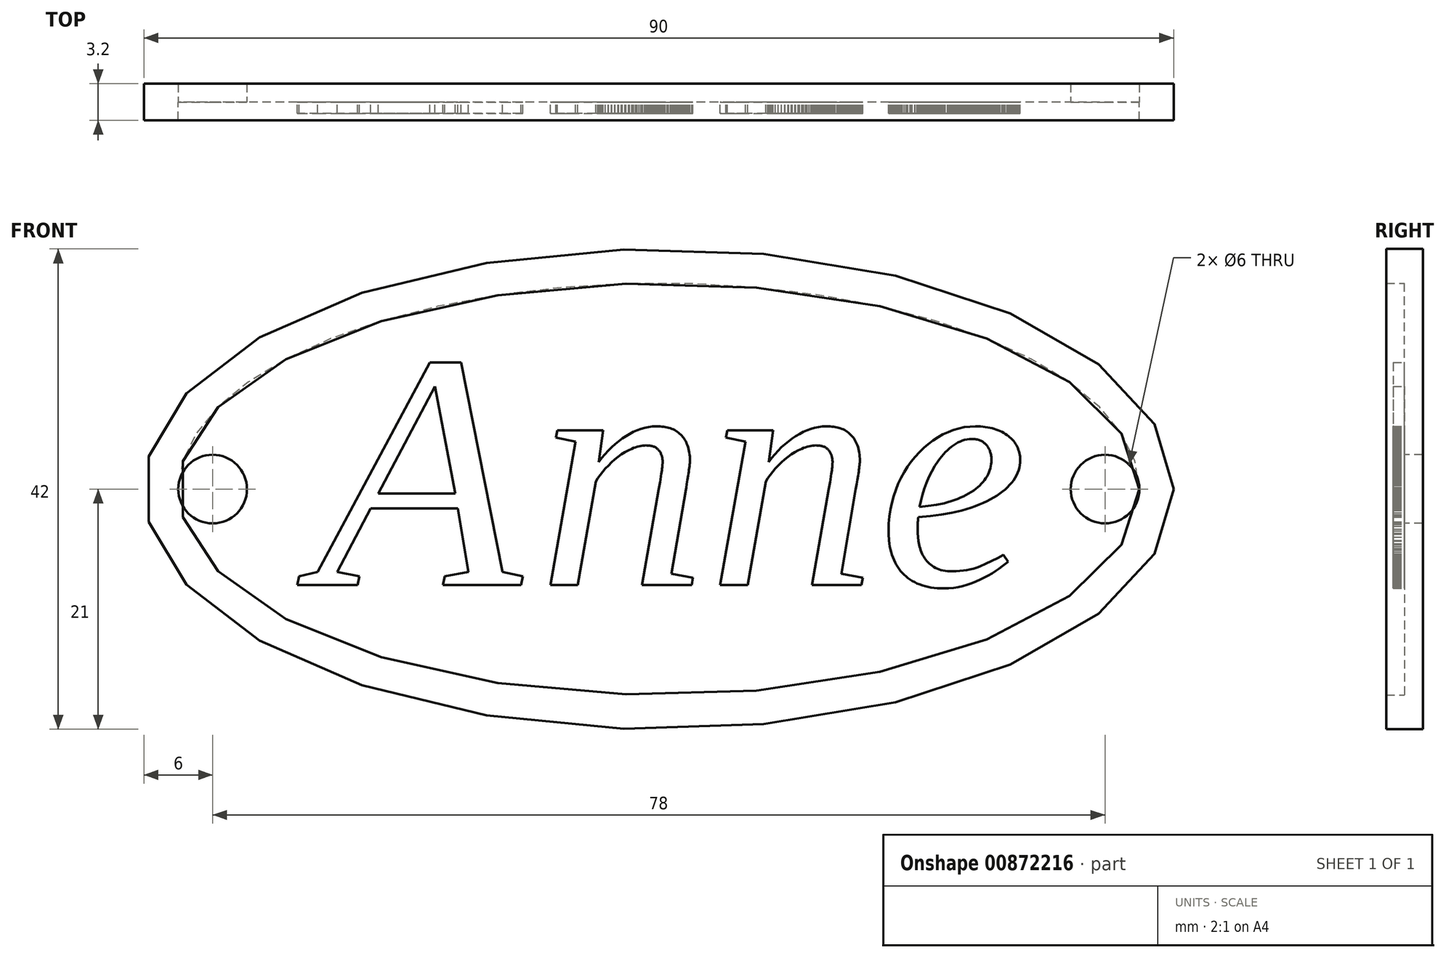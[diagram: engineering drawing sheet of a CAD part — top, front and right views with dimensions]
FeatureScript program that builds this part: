
annotation { "Feature Type Name" : "Feature", "Feature Type Description" : "" }
export const myFeature = defineFeature(function(context is Context, id is Id, definition is map)
    precondition{}
    {
        {
            var Q0;
            Q0=qCreatedBy(makeId("Front.planeOp"),FACE);
            var sketch = newSketch(context, id + "F0", { "sketchPlane" : qUnion([Q0])});
            skEllipse(sketch, "E0", {"center": v(0, 0) * mm, "majorRadius": 42 * mm, "minorRadius": 18 * mm, "majorAxis": v(1, 0)});
            skEllipse(sketch, "E1", {"center": v(0, 0) * mm, "majorRadius": 45 * mm, "minorRadius": 21 * mm, "majorAxis": v(1, 0)});
            skLineSegment(sketch, "E2", {"start": v(-81.12, 0) * mm, "end": v(85, 0) * mm, "construction": true});
            skPoint(sketch, "E2.startSnap0", {"position": v(-45, 0) * mm});
            skPoint(sketch, "E2.endSnap0", {"position": v(45, 0) * mm});
            skCircle(sketch, "E3", {"center": v(-39, 0) * mm, "radius": 3 * mm});
            skCircle(sketch, "E4", {"center": v(39, 0) * mm, "radius": 3 * mm});
            skLineSegment(sketch, "E5", {"start": v(-26.18, -7.64) * mm, "end": v(-26.32, -8.4) * mm});
            skLineSegment(sketch, "E6", {"start": v(-26.32, -8.4) * mm, "end": v(-31.6, -8.4) * mm});
            skLineSegment(sketch, "E7", {"start": v(-31.6, -8.4) * mm, "end": v(-31.45, -7.64) * mm});
            skLineSegment(sketch, "E8", {"start": v(-31.45, -7.64) * mm, "end": v(-29.84, -7.25) * mm});
            skLineSegment(sketch, "E9", {"start": v(-29.84, -7.25) * mm, "end": v(-20.02, 11.06) * mm});
            skLineSegment(sketch, "E10", {"start": v(-20.02, 11.06) * mm, "end": v(-17.27, 11.06) * mm});
            skLineSegment(sketch, "E11", {"start": v(-17.27, 11.06) * mm, "end": v(-13.67, -7.25) * mm});
            skLineSegment(sketch, "E12", {"start": v(-13.67, -7.25) * mm, "end": v(-11.87, -7.64) * mm});
            skLineSegment(sketch, "E13", {"start": v(-11.87, -7.64) * mm, "end": v(-12.03, -8.4) * mm});
            skLineSegment(sketch, "E14", {"start": v(-12.03, -8.4) * mm, "end": v(-18.87, -8.4) * mm});
            skLineSegment(sketch, "E15", {"start": v(-18.87, -8.4) * mm, "end": v(-18.71, -7.64) * mm});
            skLineSegment(sketch, "E16", {"start": v(-18.71, -7.64) * mm, "end": v(-16.65, -7.25) * mm});
            skLineSegment(sketch, "E17", {"start": v(-16.65, -7.25) * mm, "end": v(-17.57, -1.68) * mm});
            skLineSegment(sketch, "E18", {"start": v(-17.57, -1.68) * mm, "end": v(-25.17, -1.68) * mm});
            skLineSegment(sketch, "E19", {"start": v(-25.17, -1.68) * mm, "end": v(-28.12, -7.25) * mm});
            skLineSegment(sketch, "E20", {"start": v(-28.12, -7.25) * mm, "end": v(-26.18, -7.64) * mm});
            skLineSegment(sketch, "E21", {"start": v(-19.57, 8.99) * mm, "end": v(-24.53, -0.38) * mm});
            skLineSegment(sketch, "E22", {"start": v(-24.53, -0.38) * mm, "end": v(-17.8, -0.38) * mm});
            skLineSegment(sketch, "E23", {"start": v(-17.8, -0.38) * mm, "end": v(-19.57, 8.99) * mm});
            skLineSegment(sketch, "E24", {"start": v(0.33, 2.37) * mm, "end": v(0.33, 2.52) * mm});
            skLineSegment(sketch, "E25", {"start": v(0.33, 2.52) * mm, "end": v(0.32, 2.6) * mm});
            skLineSegment(sketch, "E26", {"start": v(0.32, 2.6) * mm, "end": v(0.3, 2.67) * mm});
            skLineSegment(sketch, "E27", {"start": v(0.3, 2.67) * mm, "end": v(0.3, 2.75) * mm});
            skLineSegment(sketch, "E28", {"start": v(0.3, 2.75) * mm, "end": v(0.28, 2.82) * mm});
            skLineSegment(sketch, "E29", {"start": v(0.28, 2.82) * mm, "end": v(0.26, 2.89) * mm});
            skLineSegment(sketch, "E30", {"start": v(0.26, 2.89) * mm, "end": v(0.24, 2.95) * mm});
            skLineSegment(sketch, "E31", {"start": v(0.24, 2.95) * mm, "end": v(0.22, 3.02) * mm});
            skLineSegment(sketch, "E32", {"start": v(0.22, 3.02) * mm, "end": v(0.2, 3.08) * mm});
            skLineSegment(sketch, "E33", {"start": v(0.2, 3.08) * mm, "end": v(0.17, 3.14) * mm});
            skLineSegment(sketch, "E34", {"start": v(0.17, 3.14) * mm, "end": v(0.14, 3.2) * mm});
            skLineSegment(sketch, "E35", {"start": v(0.14, 3.2) * mm, "end": v(0.1, 3.26) * mm});
            skLineSegment(sketch, "E36", {"start": v(0.1, 3.26) * mm, "end": v(0.07, 3.31) * mm});
            skLineSegment(sketch, "E37", {"start": v(0.07, 3.31) * mm, "end": v(0.03, 3.36) * mm});
            skLineSegment(sketch, "E38", {"start": v(0.03, 3.36) * mm, "end": v(-0.01, 3.42) * mm});
            skLineSegment(sketch, "E39", {"start": v(-0.01, 3.42) * mm, "end": v(-0.06, 3.46) * mm});
            skLineSegment(sketch, "E40", {"start": v(-0.06, 3.46) * mm, "end": v(-0.1, 3.51) * mm});
            skLineSegment(sketch, "E41", {"start": v(-0.1, 3.51) * mm, "end": v(-0.16, 3.55) * mm});
            skLineSegment(sketch, "E42", {"start": v(-0.16, 3.55) * mm, "end": v(-0.21, 3.6) * mm});
            skLineSegment(sketch, "E43", {"start": v(-0.21, 3.6) * mm, "end": v(-0.27, 3.63) * mm});
            skLineSegment(sketch, "E44", {"start": v(-0.27, 3.63) * mm, "end": v(-0.33, 3.66) * mm});
            skLineSegment(sketch, "E45", {"start": v(-0.33, 3.66) * mm, "end": v(-0.4, 3.7) * mm});
            skLineSegment(sketch, "E46", {"start": v(-0.4, 3.7) * mm, "end": v(-0.46, 3.72) * mm});
            skLineSegment(sketch, "E47", {"start": v(-0.46, 3.72) * mm, "end": v(-0.53, 3.74) * mm});
            skLineSegment(sketch, "E48", {"start": v(-0.53, 3.74) * mm, "end": v(-0.6, 3.76) * mm});
            skLineSegment(sketch, "E49", {"start": v(-0.6, 3.76) * mm, "end": v(-0.68, 3.78) * mm});
            skLineSegment(sketch, "E50", {"start": v(-0.68, 3.78) * mm, "end": v(-0.76, 3.8) * mm});
            skLineSegment(sketch, "E51", {"start": v(-0.76, 3.8) * mm, "end": v(-0.84, 3.8) * mm});
            skLineSegment(sketch, "E52", {"start": v(-0.84, 3.8) * mm, "end": v(-0.93, 3.81) * mm});
            skLineSegment(sketch, "E53", {"start": v(-0.93, 3.81) * mm, "end": v(-1.02, 3.82) * mm});
            skLineSegment(sketch, "E54", {"start": v(-1.02, 3.82) * mm, "end": v(-1.1, 3.82) * mm});
            skLineSegment(sketch, "E55", {"start": v(-1.1, 3.82) * mm, "end": v(-1.26, 3.81) * mm});
            skLineSegment(sketch, "E56", {"start": v(-1.26, 3.81) * mm, "end": v(-1.41, 3.8) * mm});
            skLineSegment(sketch, "E57", {"start": v(-1.41, 3.8) * mm, "end": v(-1.57, 3.78) * mm});
            skLineSegment(sketch, "E58", {"start": v(-1.57, 3.78) * mm, "end": v(-1.72, 3.75) * mm});
            skLineSegment(sketch, "E59", {"start": v(-1.72, 3.75) * mm, "end": v(-1.88, 3.7) * mm});
            skLineSegment(sketch, "E60", {"start": v(-1.88, 3.7) * mm, "end": v(-2.03, 3.66) * mm});
            skLineSegment(sketch, "E61", {"start": v(-2.03, 3.66) * mm, "end": v(-2.19, 3.6) * mm});
            skLineSegment(sketch, "E62", {"start": v(-2.19, 3.6) * mm, "end": v(-2.35, 3.53) * mm});
            skLineSegment(sketch, "E63", {"start": v(-2.35, 3.53) * mm, "end": v(-2.66, 3.38) * mm});
            skLineSegment(sketch, "E64", {"start": v(-2.66, 3.38) * mm, "end": v(-2.97, 3.21) * mm});
            skLineSegment(sketch, "E65", {"start": v(-2.97, 3.21) * mm, "end": v(-3.27, 3.02) * mm});
            skLineSegment(sketch, "E66", {"start": v(-3.27, 3.02) * mm, "end": v(-3.57, 2.81) * mm});
            skLineSegment(sketch, "E67", {"start": v(-3.57, 2.81) * mm, "end": v(-3.86, 2.58) * mm});
            skLineSegment(sketch, "E68", {"start": v(-3.86, 2.58) * mm, "end": v(-4.14, 2.33) * mm});
            skLineSegment(sketch, "E69", {"start": v(-4.14, 2.33) * mm, "end": v(-4.4, 2.07) * mm});
            skLineSegment(sketch, "E70", {"start": v(-4.4, 2.07) * mm, "end": v(-4.66, 1.79) * mm});
            skLineSegment(sketch, "E71", {"start": v(-4.66, 1.79) * mm, "end": v(-4.9, 1.5) * mm});
            skLineSegment(sketch, "E72", {"start": v(-4.9, 1.5) * mm, "end": v(-5.13, 1.23) * mm});
            skLineSegment(sketch, "E73", {"start": v(-5.13, 1.23) * mm, "end": v(-5.33, 0.95) * mm});
            skLineSegment(sketch, "E74", {"start": v(-5.33, 0.95) * mm, "end": v(-5.51, 0.67) * mm});
            skLineSegment(sketch, "E75", {"start": v(-5.51, 0.67) * mm, "end": v(-7.1, -8.4) * mm});
            skLineSegment(sketch, "E76", {"start": v(-7.1, -8.4) * mm, "end": v(-9.48, -8.4) * mm});
            skLineSegment(sketch, "E77", {"start": v(-9.48, -8.4) * mm, "end": v(-7.28, 4.14) * mm});
            skLineSegment(sketch, "E78", {"start": v(-7.28, 4.14) * mm, "end": v(-8.98, 4.5) * mm});
            skLineSegment(sketch, "E79", {"start": v(-8.98, 4.5) * mm, "end": v(-8.87, 5.14) * mm});
            skLineSegment(sketch, "E80", {"start": v(-8.87, 5.14) * mm, "end": v(-4.86, 5.14) * mm});
            skLineSegment(sketch, "E81", {"start": v(-4.86, 5.14) * mm, "end": v(-5.25, 2.38) * mm});
            skLineSegment(sketch, "E82", {"start": v(-5.25, 2.38) * mm, "end": v(-4.98, 2.72) * mm});
            skLineSegment(sketch, "E83", {"start": v(-4.98, 2.72) * mm, "end": v(-4.4, 3.36) * mm});
            skLineSegment(sketch, "E84", {"start": v(-4.4, 3.36) * mm, "end": v(-4.12, 3.66) * mm});
            skLineSegment(sketch, "E85", {"start": v(-4.12, 3.66) * mm, "end": v(-3.81, 3.94) * mm});
            skLineSegment(sketch, "E86", {"start": v(-3.81, 3.94) * mm, "end": v(-3.5, 4.2) * mm});
            skLineSegment(sketch, "E87", {"start": v(-3.5, 4.2) * mm, "end": v(-3.2, 4.43) * mm});
            skLineSegment(sketch, "E88", {"start": v(-3.2, 4.43) * mm, "end": v(-2.88, 4.64) * mm});
            skLineSegment(sketch, "E89", {"start": v(-2.88, 4.64) * mm, "end": v(-2.55, 4.83) * mm});
            skLineSegment(sketch, "E90", {"start": v(-2.55, 4.83) * mm, "end": v(-2.23, 5) * mm});
            skLineSegment(sketch, "E91", {"start": v(-2.23, 5) * mm, "end": v(-1.9, 5.14) * mm});
            skLineSegment(sketch, "E92", {"start": v(-1.9, 5.14) * mm, "end": v(-1.57, 5.26) * mm});
            skLineSegment(sketch, "E93", {"start": v(-1.57, 5.26) * mm, "end": v(-1.23, 5.36) * mm});
            skLineSegment(sketch, "E94", {"start": v(-1.23, 5.36) * mm, "end": v(-0.89, 5.43) * mm});
            skLineSegment(sketch, "E95", {"start": v(-0.89, 5.43) * mm, "end": v(-0.55, 5.47) * mm});
            skLineSegment(sketch, "E96", {"start": v(-0.55, 5.47) * mm, "end": v(-0.2, 5.49) * mm});
            skLineSegment(sketch, "E97", {"start": v(-0.2, 5.49) * mm, "end": v(0.12, 5.48) * mm});
            skLineSegment(sketch, "E98", {"start": v(0.12, 5.48) * mm, "end": v(0.28, 5.46) * mm});
            skLineSegment(sketch, "E99", {"start": v(0.28, 5.46) * mm, "end": v(0.43, 5.45) * mm});
            skLineSegment(sketch, "E100", {"start": v(0.43, 5.45) * mm, "end": v(0.58, 5.42) * mm});
            skLineSegment(sketch, "E101", {"start": v(0.58, 5.42) * mm, "end": v(0.72, 5.4) * mm});
            skLineSegment(sketch, "E102", {"start": v(0.72, 5.4) * mm, "end": v(0.86, 5.36) * mm});
            skLineSegment(sketch, "E103", {"start": v(0.86, 5.36) * mm, "end": v(1, 5.32) * mm});
            skLineSegment(sketch, "E104", {"start": v(1, 5.32) * mm, "end": v(1.13, 5.27) * mm});
            skLineSegment(sketch, "E105", {"start": v(1.13, 5.27) * mm, "end": v(1.26, 5.22) * mm});
            skLineSegment(sketch, "E106", {"start": v(1.26, 5.22) * mm, "end": v(1.38, 5.16) * mm});
            skLineSegment(sketch, "E107", {"start": v(1.38, 5.16) * mm, "end": v(1.5, 5.1) * mm});
            skLineSegment(sketch, "E108", {"start": v(1.5, 5.1) * mm, "end": v(1.6, 5.02) * mm});
            skLineSegment(sketch, "E109", {"start": v(1.6, 5.02) * mm, "end": v(1.72, 4.94) * mm});
            skLineSegment(sketch, "E110", {"start": v(1.72, 4.94) * mm, "end": v(1.82, 4.86) * mm});
            skLineSegment(sketch, "E111", {"start": v(1.82, 4.86) * mm, "end": v(1.91, 4.77) * mm});
            skLineSegment(sketch, "E112", {"start": v(1.91, 4.77) * mm, "end": v(2, 4.67) * mm});
            skLineSegment(sketch, "E113", {"start": v(2, 4.67) * mm, "end": v(2.1, 4.57) * mm});
            skLineSegment(sketch, "E114", {"start": v(2.1, 4.57) * mm, "end": v(2.18, 4.46) * mm});
            skLineSegment(sketch, "E115", {"start": v(2.18, 4.46) * mm, "end": v(2.26, 4.34) * mm});
            skLineSegment(sketch, "E116", {"start": v(2.26, 4.34) * mm, "end": v(2.33, 4.22) * mm});
            skLineSegment(sketch, "E117", {"start": v(2.33, 4.22) * mm, "end": v(2.4, 4.1) * mm});
            skLineSegment(sketch, "E118", {"start": v(2.4, 4.1) * mm, "end": v(2.45, 3.96) * mm});
            skLineSegment(sketch, "E119", {"start": v(2.45, 3.96) * mm, "end": v(2.5, 3.82) * mm});
            skLineSegment(sketch, "E120", {"start": v(2.5, 3.82) * mm, "end": v(2.55, 3.67) * mm});
            skLineSegment(sketch, "E121", {"start": v(2.55, 3.67) * mm, "end": v(2.6, 3.52) * mm});
            skLineSegment(sketch, "E122", {"start": v(2.6, 3.52) * mm, "end": v(2.64, 3.36) * mm});
            skLineSegment(sketch, "E123", {"start": v(2.64, 3.36) * mm, "end": v(2.67, 3.19) * mm});
            skLineSegment(sketch, "E124", {"start": v(2.67, 3.19) * mm, "end": v(2.69, 3.01) * mm});
            skLineSegment(sketch, "E125", {"start": v(2.69, 3.01) * mm, "end": v(2.7, 2.83) * mm});
            skLineSegment(sketch, "E126", {"start": v(2.7, 2.83) * mm, "end": v(2.72, 2.65) * mm});
            skLineSegment(sketch, "E127", {"start": v(2.72, 2.65) * mm, "end": v(2.72, 2.45) * mm});
            skLineSegment(sketch, "E128", {"start": v(2.72, 2.45) * mm, "end": v(2.72, 2.43) * mm});
            skLineSegment(sketch, "E129", {"start": v(2.72, 2.43) * mm, "end": v(2.72, 2.4) * mm});
            skLineSegment(sketch, "E130", {"start": v(2.72, 2.4) * mm, "end": v(2.72, 2.36) * mm});
            skLineSegment(sketch, "E131", {"start": v(2.72, 2.36) * mm, "end": v(2.71, 2.3) * mm});
            skLineSegment(sketch, "E132", {"start": v(2.71, 2.3) * mm, "end": v(2.7, 2.25) * mm});
            skLineSegment(sketch, "E133", {"start": v(2.7, 2.25) * mm, "end": v(2.7, 2.19) * mm});
            skLineSegment(sketch, "E134", {"start": v(2.7, 2.19) * mm, "end": v(2.7, 2.12) * mm});
            skLineSegment(sketch, "E135", {"start": v(2.7, 2.12) * mm, "end": v(2.69, 2.05) * mm});
            skLineSegment(sketch, "E136", {"start": v(2.69, 2.05) * mm, "end": v(2.68, 1.98) * mm});
            skLineSegment(sketch, "E137", {"start": v(2.68, 1.98) * mm, "end": v(2.66, 1.83) * mm});
            skLineSegment(sketch, "E138", {"start": v(2.66, 1.83) * mm, "end": v(2.64, 1.67) * mm});
            skLineSegment(sketch, "E139", {"start": v(2.64, 1.67) * mm, "end": v(2.62, 1.51) * mm});
            skLineSegment(sketch, "E140", {"start": v(2.62, 1.51) * mm, "end": v(2.6, 1.34) * mm});
            skLineSegment(sketch, "E141", {"start": v(2.6, 1.34) * mm, "end": v(2.56, 1.17) * mm});
            skLineSegment(sketch, "E142", {"start": v(2.56, 1.17) * mm, "end": v(2.5, 0.8) * mm});
            skLineSegment(sketch, "E143", {"start": v(2.5, 0.8) * mm, "end": v(2.48, 0.62) * mm});
            skLineSegment(sketch, "E144", {"start": v(2.48, 0.62) * mm, "end": v(2.45, 0.45) * mm});
            skLineSegment(sketch, "E145", {"start": v(2.45, 0.45) * mm, "end": v(2.39, 0.1) * mm});
            skLineSegment(sketch, "E146", {"start": v(2.39, 0.1) * mm, "end": v(2.36, -0.05) * mm});
            skLineSegment(sketch, "E147", {"start": v(2.36, -0.05) * mm, "end": v(1.1, -7.4) * mm});
            skLineSegment(sketch, "E148", {"start": v(1.1, -7.4) * mm, "end": v(2.98, -7.75) * mm});
            skLineSegment(sketch, "E149", {"start": v(2.98, -7.75) * mm, "end": v(2.86, -8.4) * mm});
            skLineSegment(sketch, "E150", {"start": v(2.86, -8.4) * mm, "end": v(-1.47, -8.4) * mm});
            skLineSegment(sketch, "E151", {"start": v(-1.47, -8.4) * mm, "end": v(0, -0.02) * mm});
            skLineSegment(sketch, "E152", {"start": v(0, -0.02) * mm, "end": v(0.03, 0.14) * mm});
            skLineSegment(sketch, "E153", {"start": v(0.03, 0.14) * mm, "end": v(0.09, 0.47) * mm});
            skLineSegment(sketch, "E154", {"start": v(0.09, 0.47) * mm, "end": v(0.11, 0.64) * mm});
            skLineSegment(sketch, "E155", {"start": v(0.11, 0.64) * mm, "end": v(0.14, 0.81) * mm});
            skLineSegment(sketch, "E156", {"start": v(0.14, 0.81) * mm, "end": v(0.2, 1.15) * mm});
            skLineSegment(sketch, "E157", {"start": v(0.2, 1.15) * mm, "end": v(0.22, 1.31) * mm});
            skLineSegment(sketch, "E158", {"start": v(0.22, 1.31) * mm, "end": v(0.24, 1.48) * mm});
            skLineSegment(sketch, "E159", {"start": v(0.24, 1.48) * mm, "end": v(0.27, 1.63) * mm});
            skLineSegment(sketch, "E160", {"start": v(0.27, 1.63) * mm, "end": v(0.29, 1.78) * mm});
            skLineSegment(sketch, "E161", {"start": v(0.29, 1.78) * mm, "end": v(0.3, 1.92) * mm});
            skLineSegment(sketch, "E162", {"start": v(0.3, 1.92) * mm, "end": v(0.3, 1.99) * mm});
            skLineSegment(sketch, "E163", {"start": v(0.3, 1.99) * mm, "end": v(0.31, 2.05) * mm});
            skLineSegment(sketch, "E164", {"start": v(0.31, 2.05) * mm, "end": v(0.32, 2.11) * mm});
            skLineSegment(sketch, "E165", {"start": v(0.32, 2.11) * mm, "end": v(0.32, 2.17) * mm});
            skLineSegment(sketch, "E166", {"start": v(0.32, 2.17) * mm, "end": v(0.33, 2.22) * mm});
            skLineSegment(sketch, "E167", {"start": v(0.33, 2.22) * mm, "end": v(0.33, 2.27) * mm});
            skLineSegment(sketch, "E168", {"start": v(0.33, 2.27) * mm, "end": v(0.33, 2.32) * mm});
            skLineSegment(sketch, "E169", {"start": v(0.33, 2.32) * mm, "end": v(0.33, 2.37) * mm});
            skLineSegment(sketch, "E170", {"start": v(15.18, 2.37) * mm, "end": v(15.18, 2.52) * mm});
            skLineSegment(sketch, "E171", {"start": v(15.18, 2.52) * mm, "end": v(15.17, 2.6) * mm});
            skLineSegment(sketch, "E172", {"start": v(15.17, 2.6) * mm, "end": v(15.16, 2.67) * mm});
            skLineSegment(sketch, "E173", {"start": v(15.16, 2.67) * mm, "end": v(15.15, 2.75) * mm});
            skLineSegment(sketch, "E174", {"start": v(15.15, 2.75) * mm, "end": v(15.14, 2.82) * mm});
            skLineSegment(sketch, "E175", {"start": v(15.14, 2.82) * mm, "end": v(15.12, 2.89) * mm});
            skLineSegment(sketch, "E176", {"start": v(15.12, 2.89) * mm, "end": v(15.1, 2.95) * mm});
            skLineSegment(sketch, "E177", {"start": v(15.1, 2.95) * mm, "end": v(15.07, 3.02) * mm});
            skLineSegment(sketch, "E178", {"start": v(15.07, 3.02) * mm, "end": v(15.05, 3.08) * mm});
            skLineSegment(sketch, "E179", {"start": v(15.05, 3.08) * mm, "end": v(15.02, 3.14) * mm});
            skLineSegment(sketch, "E180", {"start": v(15.02, 3.14) * mm, "end": v(14.99, 3.2) * mm});
            skLineSegment(sketch, "E181", {"start": v(14.99, 3.2) * mm, "end": v(14.96, 3.26) * mm});
            skLineSegment(sketch, "E182", {"start": v(14.96, 3.26) * mm, "end": v(14.92, 3.31) * mm});
            skLineSegment(sketch, "E183", {"start": v(14.92, 3.31) * mm, "end": v(14.88, 3.36) * mm});
            skLineSegment(sketch, "E184", {"start": v(14.88, 3.36) * mm, "end": v(14.84, 3.42) * mm});
            skLineSegment(sketch, "E185", {"start": v(14.84, 3.42) * mm, "end": v(14.8, 3.46) * mm});
            skLineSegment(sketch, "E186", {"start": v(14.8, 3.46) * mm, "end": v(14.75, 3.51) * mm});
            skLineSegment(sketch, "E187", {"start": v(14.75, 3.51) * mm, "end": v(14.7, 3.55) * mm});
            skLineSegment(sketch, "E188", {"start": v(14.7, 3.55) * mm, "end": v(14.64, 3.6) * mm});
            skLineSegment(sketch, "E189", {"start": v(14.64, 3.6) * mm, "end": v(14.58, 3.63) * mm});
            skLineSegment(sketch, "E190", {"start": v(14.58, 3.63) * mm, "end": v(14.52, 3.66) * mm});
            skLineSegment(sketch, "E191", {"start": v(14.52, 3.66) * mm, "end": v(14.46, 3.7) * mm});
            skLineSegment(sketch, "E192", {"start": v(14.46, 3.7) * mm, "end": v(14.4, 3.72) * mm});
            skLineSegment(sketch, "E193", {"start": v(14.4, 3.72) * mm, "end": v(14.32, 3.74) * mm});
            skLineSegment(sketch, "E194", {"start": v(14.32, 3.74) * mm, "end": v(14.25, 3.76) * mm});
            skLineSegment(sketch, "E195", {"start": v(14.25, 3.76) * mm, "end": v(14.17, 3.78) * mm});
            skLineSegment(sketch, "E196", {"start": v(14.17, 3.78) * mm, "end": v(14.1, 3.8) * mm});
            skLineSegment(sketch, "E197", {"start": v(14.1, 3.8) * mm, "end": v(14.01, 3.8) * mm});
            skLineSegment(sketch, "E198", {"start": v(14.01, 3.8) * mm, "end": v(13.93, 3.81) * mm});
            skLineSegment(sketch, "E199", {"start": v(13.93, 3.81) * mm, "end": v(13.84, 3.82) * mm});
            skLineSegment(sketch, "E200", {"start": v(13.84, 3.82) * mm, "end": v(13.74, 3.82) * mm});
            skLineSegment(sketch, "E201", {"start": v(13.74, 3.82) * mm, "end": v(13.6, 3.81) * mm});
            skLineSegment(sketch, "E202", {"start": v(13.6, 3.81) * mm, "end": v(13.44, 3.8) * mm});
            skLineSegment(sketch, "E203", {"start": v(13.44, 3.8) * mm, "end": v(13.29, 3.78) * mm});
            skLineSegment(sketch, "E204", {"start": v(13.29, 3.78) * mm, "end": v(13.13, 3.75) * mm});
            skLineSegment(sketch, "E205", {"start": v(13.13, 3.75) * mm, "end": v(12.98, 3.7) * mm});
            skLineSegment(sketch, "E206", {"start": v(12.98, 3.7) * mm, "end": v(12.82, 3.66) * mm});
            skLineSegment(sketch, "E207", {"start": v(12.82, 3.66) * mm, "end": v(12.67, 3.6) * mm});
            skLineSegment(sketch, "E208", {"start": v(12.67, 3.6) * mm, "end": v(12.5, 3.53) * mm});
            skLineSegment(sketch, "E209", {"start": v(12.5, 3.53) * mm, "end": v(12.2, 3.38) * mm});
            skLineSegment(sketch, "E210", {"start": v(12.2, 3.38) * mm, "end": v(11.88, 3.21) * mm});
            skLineSegment(sketch, "E211", {"start": v(11.88, 3.21) * mm, "end": v(11.58, 3.02) * mm});
            skLineSegment(sketch, "E212", {"start": v(11.58, 3.02) * mm, "end": v(11.28, 2.81) * mm});
            skLineSegment(sketch, "E213", {"start": v(11.28, 2.81) * mm, "end": v(11, 2.58) * mm});
            skLineSegment(sketch, "E214", {"start": v(11, 2.58) * mm, "end": v(10.72, 2.33) * mm});
            skLineSegment(sketch, "E215", {"start": v(10.72, 2.33) * mm, "end": v(10.45, 2.07) * mm});
            skLineSegment(sketch, "E216", {"start": v(10.45, 2.07) * mm, "end": v(10.19, 1.79) * mm});
            skLineSegment(sketch, "E217", {"start": v(10.2, 1.79) * mm, "end": v(9.95, 1.5) * mm});
            skLineSegment(sketch, "E218", {"start": v(9.95, 1.5) * mm, "end": v(9.73, 1.23) * mm});
            skLineSegment(sketch, "E219", {"start": v(9.73, 1.23) * mm, "end": v(9.52, 0.95) * mm});
            skLineSegment(sketch, "E220", {"start": v(9.52, 0.95) * mm, "end": v(9.34, 0.67) * mm});
            skLineSegment(sketch, "E221", {"start": v(9.34, 0.67) * mm, "end": v(7.76, -8.4) * mm});
            skLineSegment(sketch, "E222", {"start": v(7.76, -8.4) * mm, "end": v(5.37, -8.4) * mm});
            skLineSegment(sketch, "E223", {"start": v(5.37, -8.4) * mm, "end": v(7.57, 4.14) * mm});
            skLineSegment(sketch, "E224", {"start": v(7.57, 4.14) * mm, "end": v(5.87, 4.5) * mm});
            skLineSegment(sketch, "E225", {"start": v(5.87, 4.5) * mm, "end": v(5.99, 5.14) * mm});
            skLineSegment(sketch, "E226", {"start": v(5.99, 5.14) * mm, "end": v(9.99, 5.14) * mm});
            skLineSegment(sketch, "E227", {"start": v(9.99, 5.14) * mm, "end": v(9.6, 2.38) * mm});
            skLineSegment(sketch, "E228", {"start": v(9.6, 2.38) * mm, "end": v(9.88, 2.72) * mm});
            skLineSegment(sketch, "E229", {"start": v(9.88, 2.72) * mm, "end": v(10.44, 3.36) * mm});
            skLineSegment(sketch, "E230", {"start": v(10.44, 3.36) * mm, "end": v(10.74, 3.66) * mm});
            skLineSegment(sketch, "E231", {"start": v(10.74, 3.66) * mm, "end": v(11.04, 3.94) * mm});
            skLineSegment(sketch, "E232", {"start": v(11.04, 3.94) * mm, "end": v(11.35, 4.2) * mm});
            skLineSegment(sketch, "E233", {"start": v(11.35, 4.2) * mm, "end": v(11.66, 4.43) * mm});
            skLineSegment(sketch, "E234", {"start": v(11.66, 4.43) * mm, "end": v(11.97, 4.64) * mm});
            skLineSegment(sketch, "E235", {"start": v(11.97, 4.64) * mm, "end": v(12.3, 4.83) * mm});
            skLineSegment(sketch, "E236", {"start": v(12.3, 4.83) * mm, "end": v(12.63, 5) * mm});
            skLineSegment(sketch, "E237", {"start": v(12.63, 5) * mm, "end": v(12.95, 5.14) * mm});
            skLineSegment(sketch, "E238", {"start": v(12.95, 5.14) * mm, "end": v(13.28, 5.26) * mm});
            skLineSegment(sketch, "E239", {"start": v(13.28, 5.26) * mm, "end": v(13.62, 5.36) * mm});
            skLineSegment(sketch, "E240", {"start": v(13.62, 5.36) * mm, "end": v(13.96, 5.43) * mm});
            skLineSegment(sketch, "E241", {"start": v(13.96, 5.43) * mm, "end": v(14.3, 5.47) * mm});
            skLineSegment(sketch, "E242", {"start": v(14.3, 5.47) * mm, "end": v(14.65, 5.49) * mm});
            skLineSegment(sketch, "E243", {"start": v(14.65, 5.49) * mm, "end": v(14.97, 5.48) * mm});
            skLineSegment(sketch, "E244", {"start": v(14.97, 5.48) * mm, "end": v(15.13, 5.46) * mm});
            skLineSegment(sketch, "E245", {"start": v(15.13, 5.46) * mm, "end": v(15.28, 5.45) * mm});
            skLineSegment(sketch, "E246", {"start": v(15.28, 5.45) * mm, "end": v(15.43, 5.42) * mm});
            skLineSegment(sketch, "E247", {"start": v(15.43, 5.42) * mm, "end": v(15.57, 5.4) * mm});
            skLineSegment(sketch, "E248", {"start": v(15.57, 5.4) * mm, "end": v(15.71, 5.36) * mm});
            skLineSegment(sketch, "E249", {"start": v(15.71, 5.36) * mm, "end": v(15.85, 5.32) * mm});
            skLineSegment(sketch, "E250", {"start": v(15.85, 5.32) * mm, "end": v(15.98, 5.27) * mm});
            skLineSegment(sketch, "E251", {"start": v(15.98, 5.27) * mm, "end": v(16.1, 5.22) * mm});
            skLineSegment(sketch, "E252", {"start": v(16.1, 5.22) * mm, "end": v(16.23, 5.16) * mm});
            skLineSegment(sketch, "E253", {"start": v(16.23, 5.16) * mm, "end": v(16.35, 5.1) * mm});
            skLineSegment(sketch, "E254", {"start": v(16.35, 5.1) * mm, "end": v(16.46, 5.02) * mm});
            skLineSegment(sketch, "E255", {"start": v(16.46, 5.02) * mm, "end": v(16.57, 4.94) * mm});
            skLineSegment(sketch, "E256", {"start": v(16.57, 4.94) * mm, "end": v(16.67, 4.86) * mm});
            skLineSegment(sketch, "E257", {"start": v(16.67, 4.86) * mm, "end": v(16.77, 4.77) * mm});
            skLineSegment(sketch, "E258", {"start": v(16.77, 4.77) * mm, "end": v(16.86, 4.67) * mm});
            skLineSegment(sketch, "E259", {"start": v(16.86, 4.67) * mm, "end": v(16.95, 4.57) * mm});
            skLineSegment(sketch, "E260", {"start": v(16.95, 4.57) * mm, "end": v(17.03, 4.46) * mm});
            skLineSegment(sketch, "E261", {"start": v(17.03, 4.46) * mm, "end": v(17.1, 4.34) * mm});
            skLineSegment(sketch, "E262", {"start": v(17.1, 4.34) * mm, "end": v(17.18, 4.22) * mm});
            skLineSegment(sketch, "E263", {"start": v(17.18, 4.22) * mm, "end": v(17.24, 4.1) * mm});
            skLineSegment(sketch, "E264", {"start": v(17.24, 4.1) * mm, "end": v(17.3, 3.96) * mm});
            skLineSegment(sketch, "E265", {"start": v(17.3, 3.96) * mm, "end": v(17.36, 3.82) * mm});
            skLineSegment(sketch, "E266", {"start": v(17.36, 3.82) * mm, "end": v(17.4, 3.67) * mm});
            skLineSegment(sketch, "E267", {"start": v(17.4, 3.67) * mm, "end": v(17.45, 3.52) * mm});
            skLineSegment(sketch, "E268", {"start": v(17.45, 3.52) * mm, "end": v(17.49, 3.36) * mm});
            skLineSegment(sketch, "E269", {"start": v(17.49, 3.36) * mm, "end": v(17.52, 3.19) * mm});
            skLineSegment(sketch, "E270", {"start": v(17.52, 3.19) * mm, "end": v(17.54, 3.01) * mm});
            skLineSegment(sketch, "E271", {"start": v(17.54, 3.01) * mm, "end": v(17.56, 2.83) * mm});
            skLineSegment(sketch, "E272", {"start": v(17.56, 2.83) * mm, "end": v(17.57, 2.65) * mm});
            skLineSegment(sketch, "E273", {"start": v(17.57, 2.65) * mm, "end": v(17.57, 2.45) * mm});
            skLineSegment(sketch, "E274", {"start": v(17.57, 2.45) * mm, "end": v(17.57, 2.43) * mm});
            skLineSegment(sketch, "E275", {"start": v(17.57, 2.43) * mm, "end": v(17.57, 2.4) * mm});
            skLineSegment(sketch, "E276", {"start": v(17.57, 2.4) * mm, "end": v(17.57, 2.36) * mm});
            skLineSegment(sketch, "E277", {"start": v(17.57, 2.36) * mm, "end": v(17.57, 2.3) * mm});
            skLineSegment(sketch, "E278", {"start": v(17.57, 2.3) * mm, "end": v(17.56, 2.25) * mm});
            skLineSegment(sketch, "E279", {"start": v(17.56, 2.25) * mm, "end": v(17.56, 2.19) * mm});
            skLineSegment(sketch, "E280", {"start": v(17.56, 2.19) * mm, "end": v(17.55, 2.12) * mm});
            skLineSegment(sketch, "E281", {"start": v(17.55, 2.12) * mm, "end": v(17.54, 2.05) * mm});
            skLineSegment(sketch, "E282", {"start": v(17.54, 2.05) * mm, "end": v(17.53, 1.98) * mm});
            skLineSegment(sketch, "E283", {"start": v(17.53, 1.98) * mm, "end": v(17.51, 1.83) * mm});
            skLineSegment(sketch, "E284", {"start": v(17.51, 1.83) * mm, "end": v(17.5, 1.67) * mm});
            skLineSegment(sketch, "E285", {"start": v(17.5, 1.67) * mm, "end": v(17.47, 1.51) * mm});
            skLineSegment(sketch, "E286", {"start": v(17.47, 1.51) * mm, "end": v(17.44, 1.34) * mm});
            skLineSegment(sketch, "E287", {"start": v(17.44, 1.34) * mm, "end": v(17.41, 1.17) * mm});
            skLineSegment(sketch, "E288", {"start": v(17.41, 1.17) * mm, "end": v(17.36, 0.8) * mm});
            skLineSegment(sketch, "E289", {"start": v(17.36, 0.8) * mm, "end": v(17.33, 0.62) * mm});
            skLineSegment(sketch, "E290", {"start": v(17.33, 0.62) * mm, "end": v(17.3, 0.45) * mm});
            skLineSegment(sketch, "E291", {"start": v(17.3, 0.45) * mm, "end": v(17.24, 0.1) * mm});
            skLineSegment(sketch, "E292", {"start": v(17.24, 0.1) * mm, "end": v(17.21, -0.05) * mm});
            skLineSegment(sketch, "E293", {"start": v(17.21, -0.05) * mm, "end": v(15.95, -7.4) * mm});
            skLineSegment(sketch, "E294", {"start": v(15.95, -7.4) * mm, "end": v(17.83, -7.75) * mm});
            skLineSegment(sketch, "E295", {"start": v(17.83, -7.75) * mm, "end": v(17.72, -8.4) * mm});
            skLineSegment(sketch, "E296", {"start": v(17.72, -8.4) * mm, "end": v(13.38, -8.4) * mm});
            skLineSegment(sketch, "E297", {"start": v(13.39, -8.4) * mm, "end": v(14.85, -0.02) * mm});
            skLineSegment(sketch, "E298", {"start": v(14.85, -0.02) * mm, "end": v(14.88, 0.14) * mm});
            skLineSegment(sketch, "E299", {"start": v(14.88, 0.14) * mm, "end": v(14.94, 0.47) * mm});
            skLineSegment(sketch, "E300", {"start": v(14.94, 0.47) * mm, "end": v(14.97, 0.64) * mm});
            skLineSegment(sketch, "E301", {"start": v(14.97, 0.64) * mm, "end": v(15, 0.81) * mm});
            skLineSegment(sketch, "E302", {"start": v(15, 0.81) * mm, "end": v(15.05, 1.15) * mm});
            skLineSegment(sketch, "E303", {"start": v(15.05, 1.15) * mm, "end": v(15.07, 1.31) * mm});
            skLineSegment(sketch, "E304", {"start": v(15.07, 1.31) * mm, "end": v(15.1, 1.48) * mm});
            skLineSegment(sketch, "E305", {"start": v(15.1, 1.48) * mm, "end": v(15.12, 1.63) * mm});
            skLineSegment(sketch, "E306", {"start": v(15.12, 1.63) * mm, "end": v(15.14, 1.78) * mm});
            skLineSegment(sketch, "E307", {"start": v(15.14, 1.78) * mm, "end": v(15.16, 1.92) * mm});
            skLineSegment(sketch, "E308", {"start": v(15.16, 1.92) * mm, "end": v(15.16, 1.99) * mm});
            skLineSegment(sketch, "E309", {"start": v(15.16, 1.99) * mm, "end": v(15.17, 2.05) * mm});
            skLineSegment(sketch, "E310", {"start": v(15.17, 2.05) * mm, "end": v(15.17, 2.11) * mm});
            skLineSegment(sketch, "E311", {"start": v(15.17, 2.11) * mm, "end": v(15.18, 2.17) * mm});
            skLineSegment(sketch, "E312", {"start": v(15.18, 2.17) * mm, "end": v(15.18, 2.22) * mm});
            skLineSegment(sketch, "E313", {"start": v(15.18, 2.22) * mm, "end": v(15.18, 2.27) * mm});
            skLineSegment(sketch, "E314", {"start": v(15.18, 2.27) * mm, "end": v(15.18, 2.32) * mm});
            skLineSegment(sketch, "E315", {"start": v(15.18, 2.32) * mm, "end": v(15.18, 2.37) * mm});
            skLineSegment(sketch, "E316", {"start": v(31.6, 2.54) * mm, "end": v(31.58, 2.3) * mm});
            skLineSegment(sketch, "E317", {"start": v(31.58, 2.3) * mm, "end": v(31.55, 2.08) * mm});
            skLineSegment(sketch, "E318", {"start": v(31.55, 2.08) * mm, "end": v(31.5, 1.85) * mm});
            skLineSegment(sketch, "E319", {"start": v(31.5, 1.85) * mm, "end": v(31.44, 1.63) * mm});
            skLineSegment(sketch, "E320", {"start": v(31.44, 1.63) * mm, "end": v(31.36, 1.4) * mm});
            skLineSegment(sketch, "E321", {"start": v(31.36, 1.4) * mm, "end": v(31.26, 1.2) * mm});
            skLineSegment(sketch, "E322", {"start": v(31.26, 1.2) * mm, "end": v(31.14, 0.98) * mm});
            skLineSegment(sketch, "E323", {"start": v(31.14, 0.98) * mm, "end": v(31, 0.77) * mm});
            skLineSegment(sketch, "E324", {"start": v(31, 0.77) * mm, "end": v(30.85, 0.56) * mm});
            skLineSegment(sketch, "E325", {"start": v(30.85, 0.56) * mm, "end": v(30.67, 0.36) * mm});
            skLineSegment(sketch, "E326", {"start": v(30.67, 0.36) * mm, "end": v(30.48, 0.16) * mm});
            skLineSegment(sketch, "E327", {"start": v(30.48, 0.16) * mm, "end": v(30.27, -0.03) * mm});
            skLineSegment(sketch, "E328", {"start": v(30.27, -0.03) * mm, "end": v(30.05, -0.21) * mm});
            skLineSegment(sketch, "E329", {"start": v(30.05, -0.21) * mm, "end": v(29.8, -0.4) * mm});
            skLineSegment(sketch, "E330", {"start": v(29.8, -0.4) * mm, "end": v(29.55, -0.57) * mm});
            skLineSegment(sketch, "E331", {"start": v(29.55, -0.57) * mm, "end": v(29.27, -0.74) * mm});
            skLineSegment(sketch, "E332", {"start": v(29.27, -0.74) * mm, "end": v(28.99, -0.9) * mm});
            skLineSegment(sketch, "E333", {"start": v(28.99, -0.9) * mm, "end": v(28.68, -1.06) * mm});
            skLineSegment(sketch, "E334", {"start": v(28.68, -1.06) * mm, "end": v(28.36, -1.21) * mm});
            skLineSegment(sketch, "E335", {"start": v(28.36, -1.21) * mm, "end": v(28.02, -1.36) * mm});
            skLineSegment(sketch, "E336", {"start": v(28.02, -1.36) * mm, "end": v(27.66, -1.5) * mm});
            skLineSegment(sketch, "E337", {"start": v(27.66, -1.5) * mm, "end": v(27.28, -1.62) * mm});
            skLineSegment(sketch, "E338", {"start": v(27.28, -1.62) * mm, "end": v(26.48, -1.87) * mm});
            skLineSegment(sketch, "E339", {"start": v(26.48, -1.87) * mm, "end": v(25.62, -2.07) * mm});
            skLineSegment(sketch, "E340", {"start": v(25.62, -2.07) * mm, "end": v(24.7, -2.24) * mm});
            skLineSegment(sketch, "E341", {"start": v(24.7, -2.24) * mm, "end": v(23.72, -2.37) * mm});
            skLineSegment(sketch, "E342", {"start": v(23.72, -2.37) * mm, "end": v(22.68, -2.46) * mm});
            skLineSegment(sketch, "E343", {"start": v(22.68, -2.46) * mm, "end": v(22.68, -2.47) * mm});
            skLineSegment(sketch, "E344", {"start": v(22.68, -2.47) * mm, "end": v(22.68, -2.5) * mm});
            skLineSegment(sketch, "E345", {"start": v(22.68, -2.5) * mm, "end": v(22.68, -2.5) * mm});
            skLineSegment(sketch, "E346", {"start": v(22.68, -2.5) * mm, "end": v(22.68, -2.53) * mm});
            skLineSegment(sketch, "E347", {"start": v(22.67, -2.53) * mm, "end": v(22.67, -2.55) * mm});
            skLineSegment(sketch, "E348", {"start": v(22.67, -2.55) * mm, "end": v(22.67, -2.57) * mm});
            skLineSegment(sketch, "E349", {"start": v(22.67, -2.57) * mm, "end": v(22.67, -2.6) * mm});
            skLineSegment(sketch, "E350", {"start": v(22.67, -2.6) * mm, "end": v(22.67, -2.62) * mm});
            skLineSegment(sketch, "E351", {"start": v(22.67, -2.62) * mm, "end": v(22.66, -2.67) * mm});
            skLineSegment(sketch, "E352", {"start": v(22.66, -2.67) * mm, "end": v(22.65, -2.73) * mm});
            skLineSegment(sketch, "E353", {"start": v(22.65, -2.73) * mm, "end": v(22.65, -2.8) * mm});
            skLineSegment(sketch, "E354", {"start": v(22.65, -2.8) * mm, "end": v(22.64, -2.86) * mm});
            skLineSegment(sketch, "E355", {"start": v(22.64, -2.86) * mm, "end": v(22.64, -2.93) * mm});
            skLineSegment(sketch, "E356", {"start": v(22.64, -2.93) * mm, "end": v(22.63, -3.08) * mm});
            skLineSegment(sketch, "E357", {"start": v(22.63, -3.08) * mm, "end": v(22.63, -3.24) * mm});
            skLineSegment(sketch, "E358", {"start": v(22.63, -3.24) * mm, "end": v(22.63, -3.41) * mm});
            skLineSegment(sketch, "E359", {"start": v(22.63, -3.41) * mm, "end": v(22.63, -3.5) * mm});
            skLineSegment(sketch, "E360", {"start": v(22.63, -3.5) * mm, "end": v(22.63, -3.86) * mm});
            skLineSegment(sketch, "E361", {"start": v(22.63, -3.86) * mm, "end": v(22.66, -4.2) * mm});
            skLineSegment(sketch, "E362", {"start": v(22.66, -4.2) * mm, "end": v(22.7, -4.54) * mm});
            skLineSegment(sketch, "E363", {"start": v(22.7, -4.54) * mm, "end": v(22.76, -4.87) * mm});
            skLineSegment(sketch, "E364", {"start": v(22.76, -4.87) * mm, "end": v(22.8, -5.04) * mm});
            skLineSegment(sketch, "E365", {"start": v(22.8, -5.04) * mm, "end": v(22.84, -5.2) * mm});
            skLineSegment(sketch, "E366", {"start": v(22.84, -5.2) * mm, "end": v(22.9, -5.35) * mm});
            skLineSegment(sketch, "E367", {"start": v(22.9, -5.35) * mm, "end": v(22.95, -5.5) * mm});
            skLineSegment(sketch, "E368", {"start": v(22.95, -5.5) * mm, "end": v(23.01, -5.65) * mm});
            skLineSegment(sketch, "E369", {"start": v(23.01, -5.65) * mm, "end": v(23.08, -5.79) * mm});
            skLineSegment(sketch, "E370", {"start": v(23.08, -5.79) * mm, "end": v(23.16, -5.92) * mm});
            skLineSegment(sketch, "E371", {"start": v(23.16, -5.92) * mm, "end": v(23.24, -6.05) * mm});
            skLineSegment(sketch, "E372", {"start": v(23.24, -6.05) * mm, "end": v(23.33, -6.18) * mm});
            skLineSegment(sketch, "E373", {"start": v(23.33, -6.18) * mm, "end": v(23.43, -6.3) * mm});
            skLineSegment(sketch, "E374", {"start": v(23.43, -6.3) * mm, "end": v(23.54, -6.41) * mm});
            skLineSegment(sketch, "E375", {"start": v(23.54, -6.41) * mm, "end": v(23.65, -6.52) * mm});
            skLineSegment(sketch, "E376", {"start": v(23.65, -6.52) * mm, "end": v(23.77, -6.62) * mm});
            skLineSegment(sketch, "E377", {"start": v(23.77, -6.62) * mm, "end": v(23.9, -6.72) * mm});
            skLineSegment(sketch, "E378", {"start": v(23.9, -6.72) * mm, "end": v(24.04, -6.8) * mm});
            skLineSegment(sketch, "E379", {"start": v(24.04, -6.8) * mm, "end": v(24.18, -6.89) * mm});
            skLineSegment(sketch, "E380", {"start": v(24.18, -6.89) * mm, "end": v(24.33, -6.96) * mm});
            skLineSegment(sketch, "E381", {"start": v(24.33, -6.96) * mm, "end": v(24.5, -7.02) * mm});
            skLineSegment(sketch, "E382", {"start": v(24.5, -7.02) * mm, "end": v(24.67, -7.07) * mm});
            skLineSegment(sketch, "E383", {"start": v(24.67, -7.07) * mm, "end": v(24.85, -7.12) * mm});
            skLineSegment(sketch, "E384", {"start": v(24.85, -7.12) * mm, "end": v(25.04, -7.15) * mm});
            skLineSegment(sketch, "E385", {"start": v(25.04, -7.15) * mm, "end": v(25.24, -7.17) * mm});
            skLineSegment(sketch, "E386", {"start": v(25.24, -7.17) * mm, "end": v(25.45, -7.19) * mm});
            skLineSegment(sketch, "E387", {"start": v(25.45, -7.19) * mm, "end": v(25.68, -7.2) * mm});
            skLineSegment(sketch, "E388", {"start": v(25.68, -7.2) * mm, "end": v(26, -7.18) * mm});
            skLineSegment(sketch, "E389", {"start": v(26, -7.18) * mm, "end": v(26.31, -7.16) * mm});
            skLineSegment(sketch, "E390", {"start": v(26.31, -7.16) * mm, "end": v(26.62, -7.13) * mm});
            skLineSegment(sketch, "E391", {"start": v(26.62, -7.13) * mm, "end": v(26.92, -7.08) * mm});
            skLineSegment(sketch, "E392", {"start": v(26.92, -7.08) * mm, "end": v(27.22, -7.02) * mm});
            skLineSegment(sketch, "E393", {"start": v(27.22, -7.02) * mm, "end": v(27.5, -6.95) * mm});
            skLineSegment(sketch, "E394", {"start": v(27.5, -6.95) * mm, "end": v(27.79, -6.86) * mm});
            skLineSegment(sketch, "E395", {"start": v(27.79, -6.86) * mm, "end": v(28.07, -6.76) * mm});
            skLineSegment(sketch, "E396", {"start": v(28.07, -6.76) * mm, "end": v(28.6, -6.53) * mm});
            skLineSegment(sketch, "E397", {"start": v(28.6, -6.53) * mm, "end": v(29.63, -6.03) * mm});
            skLineSegment(sketch, "E398", {"start": v(29.63, -6.03) * mm, "end": v(30.1, -5.75) * mm});
            skLineSegment(sketch, "E399", {"start": v(30.1, -5.75) * mm, "end": v(30.53, -6.36) * mm});
            skLineSegment(sketch, "E400", {"start": v(30.53, -6.36) * mm, "end": v(30.29, -6.55) * mm});
            skLineSegment(sketch, "E401", {"start": v(30.29, -6.55) * mm, "end": v(30.03, -6.75) * mm});
            skLineSegment(sketch, "E402", {"start": v(30.03, -6.75) * mm, "end": v(29.75, -6.96) * mm});
            skLineSegment(sketch, "E403", {"start": v(29.75, -6.96) * mm, "end": v(29.45, -7.16) * mm});
            skLineSegment(sketch, "E404", {"start": v(29.45, -7.16) * mm, "end": v(29.13, -7.37) * mm});
            skLineSegment(sketch, "E405", {"start": v(29.13, -7.37) * mm, "end": v(28.8, -7.56) * mm});
            skLineSegment(sketch, "E406", {"start": v(28.8, -7.56) * mm, "end": v(28.1, -7.93) * mm});
            skLineSegment(sketch, "E407", {"start": v(28.1, -7.93) * mm, "end": v(27.73, -8.08) * mm});
            skLineSegment(sketch, "E408", {"start": v(27.73, -8.08) * mm, "end": v(27.35, -8.23) * mm});
            skLineSegment(sketch, "E409", {"start": v(27.35, -8.23) * mm, "end": v(26.97, -8.36) * mm});
            skLineSegment(sketch, "E410", {"start": v(26.97, -8.36) * mm, "end": v(26.57, -8.47) * mm});
            skLineSegment(sketch, "E411", {"start": v(26.57, -8.47) * mm, "end": v(26.16, -8.57) * mm});
            skLineSegment(sketch, "E412", {"start": v(26.16, -8.57) * mm, "end": v(25.76, -8.63) * mm});
            skLineSegment(sketch, "E413", {"start": v(25.76, -8.63) * mm, "end": v(25.34, -8.67) * mm});
            skLineSegment(sketch, "E414", {"start": v(25.34, -8.67) * mm, "end": v(24.93, -8.69) * mm});
            skLineSegment(sketch, "E415", {"start": v(24.93, -8.69) * mm, "end": v(24.63, -8.68) * mm});
            skLineSegment(sketch, "E416", {"start": v(24.63, -8.68) * mm, "end": v(24.34, -8.67) * mm});
            skLineSegment(sketch, "E417", {"start": v(24.34, -8.67) * mm, "end": v(24.06, -8.64) * mm});
            skLineSegment(sketch, "E418", {"start": v(24.06, -8.64) * mm, "end": v(23.78, -8.6) * mm});
            skLineSegment(sketch, "E419", {"start": v(23.78, -8.6) * mm, "end": v(23.52, -8.55) * mm});
            skLineSegment(sketch, "E420", {"start": v(23.52, -8.55) * mm, "end": v(23.27, -8.5) * mm});
            skLineSegment(sketch, "E421", {"start": v(23.27, -8.5) * mm, "end": v(23.03, -8.42) * mm});
            skLineSegment(sketch, "E422", {"start": v(23.03, -8.42) * mm, "end": v(22.8, -8.34) * mm});
            skLineSegment(sketch, "E423", {"start": v(22.8, -8.34) * mm, "end": v(22.58, -8.25) * mm});
            skLineSegment(sketch, "E424", {"start": v(22.58, -8.25) * mm, "end": v(22.36, -8.14) * mm});
            skLineSegment(sketch, "E425", {"start": v(22.36, -8.14) * mm, "end": v(22.16, -8.03) * mm});
            skLineSegment(sketch, "E426", {"start": v(22.16, -8.03) * mm, "end": v(21.97, -7.91) * mm});
            skLineSegment(sketch, "E427", {"start": v(21.97, -7.91) * mm, "end": v(21.78, -7.78) * mm});
            skLineSegment(sketch, "E428", {"start": v(21.78, -7.78) * mm, "end": v(21.6, -7.64) * mm});
            skLineSegment(sketch, "E429", {"start": v(21.6, -7.64) * mm, "end": v(21.44, -7.5) * mm});
            skLineSegment(sketch, "E430", {"start": v(21.44, -7.5) * mm, "end": v(21.29, -7.34) * mm});
            skLineSegment(sketch, "E431", {"start": v(21.29, -7.34) * mm, "end": v(21.14, -7.17) * mm});
            skLineSegment(sketch, "E432", {"start": v(21.14, -7.17) * mm, "end": v(21, -7) * mm});
            skLineSegment(sketch, "E433", {"start": v(21, -7) * mm, "end": v(20.88, -6.8) * mm});
            skLineSegment(sketch, "E434", {"start": v(20.88, -6.8) * mm, "end": v(20.76, -6.62) * mm});
            skLineSegment(sketch, "E435", {"start": v(20.76, -6.62) * mm, "end": v(20.65, -6.41) * mm});
            skLineSegment(sketch, "E436", {"start": v(20.65, -6.41) * mm, "end": v(20.55, -6.2) * mm});
            skLineSegment(sketch, "E437", {"start": v(20.55, -6.2) * mm, "end": v(20.46, -5.98) * mm});
            skLineSegment(sketch, "E438", {"start": v(20.46, -5.98) * mm, "end": v(20.38, -5.75) * mm});
            skLineSegment(sketch, "E439", {"start": v(20.38, -5.75) * mm, "end": v(20.3, -5.51) * mm});
            skLineSegment(sketch, "E440", {"start": v(20.3, -5.51) * mm, "end": v(20.25, -5.27) * mm});
            skLineSegment(sketch, "E441", {"start": v(20.25, -5.27) * mm, "end": v(20.2, -5.02) * mm});
            skLineSegment(sketch, "E442", {"start": v(20.2, -5.02) * mm, "end": v(20.15, -4.76) * mm});
            skLineSegment(sketch, "E443", {"start": v(20.15, -4.76) * mm, "end": v(20.12, -4.5) * mm});
            skLineSegment(sketch, "E444", {"start": v(20.12, -4.5) * mm, "end": v(20.08, -3.94) * mm});
            skLineSegment(sketch, "E445", {"start": v(20.08, -3.94) * mm, "end": v(20.08, -3.65) * mm});
            skLineSegment(sketch, "E446", {"start": v(20.08, -3.65) * mm, "end": v(20.1, -3.02) * mm});
            skLineSegment(sketch, "E447", {"start": v(20.1, -3.02) * mm, "end": v(20.15, -2.4) * mm});
            skLineSegment(sketch, "E448", {"start": v(20.15, -2.4) * mm, "end": v(20.24, -1.8) * mm});
            skLineSegment(sketch, "E449", {"start": v(20.24, -1.8) * mm, "end": v(20.37, -1.2) * mm});
            skLineSegment(sketch, "E450", {"start": v(20.37, -1.2) * mm, "end": v(20.52, -0.62) * mm});
            skLineSegment(sketch, "E451", {"start": v(20.52, -0.62) * mm, "end": v(20.71, -0.07) * mm});
            skLineSegment(sketch, "E452", {"start": v(20.71, -0.07) * mm, "end": v(20.93, 0.47) * mm});
            skLineSegment(sketch, "E453", {"start": v(20.93, 0.47) * mm, "end": v(21.17, 0.98) * mm});
            skLineSegment(sketch, "E454", {"start": v(21.17, 0.98) * mm, "end": v(21.44, 1.48) * mm});
            skLineSegment(sketch, "E455", {"start": v(21.44, 1.48) * mm, "end": v(21.74, 1.96) * mm});
            skLineSegment(sketch, "E456", {"start": v(21.74, 1.96) * mm, "end": v(22.06, 2.4) * mm});
            skLineSegment(sketch, "E457", {"start": v(22.06, 2.4) * mm, "end": v(22.4, 2.83) * mm});
            skLineSegment(sketch, "E458", {"start": v(22.4, 2.83) * mm, "end": v(22.78, 3.23) * mm});
            skLineSegment(sketch, "E459", {"start": v(22.78, 3.23) * mm, "end": v(23.16, 3.6) * mm});
            skLineSegment(sketch, "E460", {"start": v(23.16, 3.6) * mm, "end": v(23.55, 3.94) * mm});
            skLineSegment(sketch, "E461", {"start": v(23.55, 3.94) * mm, "end": v(23.96, 4.25) * mm});
            skLineSegment(sketch, "E462", {"start": v(23.96, 4.25) * mm, "end": v(24.4, 4.53) * mm});
            skLineSegment(sketch, "E463", {"start": v(24.4, 4.53) * mm, "end": v(24.83, 4.77) * mm});
            skLineSegment(sketch, "E464", {"start": v(24.83, 4.77) * mm, "end": v(25.29, 4.98) * mm});
            skLineSegment(sketch, "E465", {"start": v(25.29, 4.98) * mm, "end": v(25.75, 5.16) * mm});
            skLineSegment(sketch, "E466", {"start": v(25.75, 5.16) * mm, "end": v(26.23, 5.3) * mm});
            skLineSegment(sketch, "E467", {"start": v(26.23, 5.3) * mm, "end": v(26.7, 5.4) * mm});
            skLineSegment(sketch, "E468", {"start": v(26.7, 5.4) * mm, "end": v(27.19, 5.47) * mm});
            skLineSegment(sketch, "E469", {"start": v(27.19, 5.47) * mm, "end": v(27.68, 5.49) * mm});
            skLineSegment(sketch, "E470", {"start": v(27.68, 5.49) * mm, "end": v(28.13, 5.47) * mm});
            skLineSegment(sketch, "E471", {"start": v(28.13, 5.47) * mm, "end": v(28.34, 5.46) * mm});
            skLineSegment(sketch, "E472", {"start": v(28.34, 5.46) * mm, "end": v(28.55, 5.43) * mm});
            skLineSegment(sketch, "E473", {"start": v(28.55, 5.43) * mm, "end": v(28.75, 5.4) * mm});
            skLineSegment(sketch, "E474", {"start": v(28.75, 5.4) * mm, "end": v(28.95, 5.36) * mm});
            skLineSegment(sketch, "E475", {"start": v(28.95, 5.36) * mm, "end": v(29.13, 5.31) * mm});
            skLineSegment(sketch, "E476", {"start": v(29.13, 5.31) * mm, "end": v(29.32, 5.26) * mm});
            skLineSegment(sketch, "E477", {"start": v(29.32, 5.26) * mm, "end": v(29.5, 5.2) * mm});
            skLineSegment(sketch, "E478", {"start": v(29.5, 5.2) * mm, "end": v(29.67, 5.14) * mm});
            skLineSegment(sketch, "E479", {"start": v(29.67, 5.14) * mm, "end": v(29.84, 5.07) * mm});
            skLineSegment(sketch, "E480", {"start": v(29.84, 5.07) * mm, "end": v(30, 5) * mm});
            skLineSegment(sketch, "E481", {"start": v(30, 5) * mm, "end": v(30.15, 4.92) * mm});
            skLineSegment(sketch, "E482", {"start": v(30.15, 4.92) * mm, "end": v(30.29, 4.83) * mm});
            skLineSegment(sketch, "E483", {"start": v(30.29, 4.83) * mm, "end": v(30.43, 4.74) * mm});
            skLineSegment(sketch, "E484", {"start": v(30.43, 4.74) * mm, "end": v(30.56, 4.64) * mm});
            skLineSegment(sketch, "E485", {"start": v(30.56, 4.64) * mm, "end": v(30.68, 4.54) * mm});
            skLineSegment(sketch, "E486", {"start": v(30.68, 4.54) * mm, "end": v(30.8, 4.44) * mm});
            skLineSegment(sketch, "E487", {"start": v(30.8, 4.44) * mm, "end": v(30.9, 4.33) * mm});
            skLineSegment(sketch, "E488", {"start": v(30.9, 4.33) * mm, "end": v(31, 4.21) * mm});
            skLineSegment(sketch, "E489", {"start": v(31, 4.21) * mm, "end": v(31.09, 4.1) * mm});
            skLineSegment(sketch, "E490", {"start": v(31.09, 4.1) * mm, "end": v(31.17, 3.97) * mm});
            skLineSegment(sketch, "E491", {"start": v(31.17, 3.97) * mm, "end": v(31.25, 3.84) * mm});
            skLineSegment(sketch, "E492", {"start": v(31.25, 3.84) * mm, "end": v(31.32, 3.7) * mm});
            skLineSegment(sketch, "E493", {"start": v(31.32, 3.7) * mm, "end": v(31.38, 3.57) * mm});
            skLineSegment(sketch, "E494", {"start": v(31.38, 3.57) * mm, "end": v(31.44, 3.43) * mm});
            skLineSegment(sketch, "E495", {"start": v(31.44, 3.43) * mm, "end": v(31.48, 3.3) * mm});
            skLineSegment(sketch, "E496", {"start": v(31.49, 3.3) * mm, "end": v(31.52, 3.15) * mm});
            skLineSegment(sketch, "E497", {"start": v(31.52, 3.15) * mm, "end": v(31.55, 3) * mm});
            skLineSegment(sketch, "E498", {"start": v(31.55, 3) * mm, "end": v(31.57, 2.85) * mm});
            skLineSegment(sketch, "E499", {"start": v(31.57, 2.85) * mm, "end": v(31.59, 2.7) * mm});
            skLineSegment(sketch, "E500", {"start": v(31.59, 2.7) * mm, "end": v(31.6, 2.54) * mm});
            skLineSegment(sketch, "E501", {"start": v(22.8, -1.55) * mm, "end": v(23.56, -1.48) * mm});
            skLineSegment(sketch, "E502", {"start": v(23.56, -1.48) * mm, "end": v(24.27, -1.37) * mm});
            skLineSegment(sketch, "E503", {"start": v(24.27, -1.37) * mm, "end": v(24.93, -1.23) * mm});
            skLineSegment(sketch, "E504", {"start": v(24.93, -1.23) * mm, "end": v(25.25, -1.15) * mm});
            skLineSegment(sketch, "E505", {"start": v(25.25, -1.15) * mm, "end": v(25.55, -1.06) * mm});
            skLineSegment(sketch, "E506", {"start": v(25.55, -1.06) * mm, "end": v(25.84, -0.96) * mm});
            skLineSegment(sketch, "E507", {"start": v(25.84, -0.96) * mm, "end": v(26.11, -0.86) * mm});
            skLineSegment(sketch, "E508", {"start": v(26.11, -0.86) * mm, "end": v(26.38, -0.75) * mm});
            skLineSegment(sketch, "E509", {"start": v(26.38, -0.75) * mm, "end": v(26.63, -0.63) * mm});
            skLineSegment(sketch, "E510", {"start": v(26.63, -0.63) * mm, "end": v(26.86, -0.51) * mm});
            skLineSegment(sketch, "E511", {"start": v(26.86, -0.51) * mm, "end": v(27.1, -0.39) * mm});
            skLineSegment(sketch, "E512", {"start": v(27.1, -0.39) * mm, "end": v(27.3, -0.26) * mm});
            skLineSegment(sketch, "E513", {"start": v(27.3, -0.26) * mm, "end": v(27.5, -0.12) * mm});
            skLineSegment(sketch, "E514", {"start": v(27.5, -0.12) * mm, "end": v(27.7, 0.02) * mm});
            skLineSegment(sketch, "E515", {"start": v(27.7, 0.02) * mm, "end": v(27.88, 0.16) * mm});
            skLineSegment(sketch, "E516", {"start": v(27.87, 0.16) * mm, "end": v(28.04, 0.31) * mm});
            skLineSegment(sketch, "E517", {"start": v(28.04, 0.31) * mm, "end": v(28.2, 0.47) * mm});
            skLineSegment(sketch, "E518", {"start": v(28.2, 0.47) * mm, "end": v(28.34, 0.62) * mm});
            skLineSegment(sketch, "E519", {"start": v(28.34, 0.62) * mm, "end": v(28.47, 0.78) * mm});
            skLineSegment(sketch, "E520", {"start": v(28.47, 0.78) * mm, "end": v(28.58, 0.95) * mm});
            skLineSegment(sketch, "E521", {"start": v(28.58, 0.95) * mm, "end": v(28.68, 1.11) * mm});
            skLineSegment(sketch, "E522", {"start": v(28.68, 1.11) * mm, "end": v(28.78, 1.29) * mm});
            skLineSegment(sketch, "E523", {"start": v(28.78, 1.29) * mm, "end": v(28.85, 1.46) * mm});
            skLineSegment(sketch, "E524", {"start": v(28.85, 1.46) * mm, "end": v(28.92, 1.64) * mm});
            skLineSegment(sketch, "E525", {"start": v(28.92, 1.64) * mm, "end": v(28.98, 1.81) * mm});
            skLineSegment(sketch, "E526", {"start": v(28.98, 1.81) * mm, "end": v(29.02, 2) * mm});
            skLineSegment(sketch, "E527", {"start": v(29.02, 2) * mm, "end": v(29.05, 2.17) * mm});
            skLineSegment(sketch, "E528", {"start": v(29.05, 2.17) * mm, "end": v(29.07, 2.36) * mm});
            skLineSegment(sketch, "E529", {"start": v(29.07, 2.36) * mm, "end": v(29.07, 2.54) * mm});
            skLineSegment(sketch, "E530", {"start": v(29.07, 2.54) * mm, "end": v(29.07, 2.73) * mm});
            skLineSegment(sketch, "E531", {"start": v(29.07, 2.73) * mm, "end": v(29.06, 2.83) * mm});
            skLineSegment(sketch, "E532", {"start": v(29.06, 2.83) * mm, "end": v(29.05, 2.92) * mm});
            skLineSegment(sketch, "E533", {"start": v(29.05, 2.92) * mm, "end": v(29.03, 3.01) * mm});
            skLineSegment(sketch, "E534", {"start": v(29.03, 3.01) * mm, "end": v(29.01, 3.1) * mm});
            skLineSegment(sketch, "E535", {"start": v(29.01, 3.1) * mm, "end": v(28.99, 3.19) * mm});
            skLineSegment(sketch, "E536", {"start": v(28.99, 3.19) * mm, "end": v(28.96, 3.27) * mm});
            skLineSegment(sketch, "E537", {"start": v(28.96, 3.27) * mm, "end": v(28.93, 3.35) * mm});
            skLineSegment(sketch, "E538", {"start": v(28.93, 3.35) * mm, "end": v(28.9, 3.43) * mm});
            skLineSegment(sketch, "E539", {"start": v(28.9, 3.43) * mm, "end": v(28.86, 3.51) * mm});
            skLineSegment(sketch, "E540", {"start": v(28.86, 3.51) * mm, "end": v(28.82, 3.58) * mm});
            skLineSegment(sketch, "E541", {"start": v(28.82, 3.58) * mm, "end": v(28.78, 3.66) * mm});
            skLineSegment(sketch, "E542", {"start": v(28.78, 3.66) * mm, "end": v(28.73, 3.73) * mm});
            skLineSegment(sketch, "E543", {"start": v(28.73, 3.73) * mm, "end": v(28.68, 3.8) * mm});
            skLineSegment(sketch, "E544", {"start": v(28.68, 3.8) * mm, "end": v(28.63, 3.86) * mm});
            skLineSegment(sketch, "E545", {"start": v(28.63, 3.86) * mm, "end": v(28.57, 3.92) * mm});
            skLineSegment(sketch, "E546", {"start": v(28.57, 3.92) * mm, "end": v(28.51, 3.98) * mm});
            skLineSegment(sketch, "E547", {"start": v(28.51, 3.98) * mm, "end": v(28.45, 4.04) * mm});
            skLineSegment(sketch, "E548", {"start": v(28.45, 4.04) * mm, "end": v(28.39, 4.09) * mm});
            skLineSegment(sketch, "E549", {"start": v(28.39, 4.09) * mm, "end": v(28.32, 4.14) * mm});
            skLineSegment(sketch, "E550", {"start": v(28.32, 4.14) * mm, "end": v(28.25, 4.18) * mm});
            skLineSegment(sketch, "E551", {"start": v(28.25, 4.18) * mm, "end": v(28.17, 4.22) * mm});
            skLineSegment(sketch, "E552", {"start": v(28.17, 4.22) * mm, "end": v(28.1, 4.25) * mm});
            skLineSegment(sketch, "E553", {"start": v(28.1, 4.25) * mm, "end": v(28.01, 4.28) * mm});
            skLineSegment(sketch, "E554", {"start": v(28.01, 4.28) * mm, "end": v(27.93, 4.3) * mm});
            skLineSegment(sketch, "E555", {"start": v(27.93, 4.3) * mm, "end": v(27.84, 4.33) * mm});
            skLineSegment(sketch, "E556", {"start": v(27.84, 4.33) * mm, "end": v(27.75, 4.35) * mm});
            skLineSegment(sketch, "E557", {"start": v(27.75, 4.35) * mm, "end": v(27.66, 4.36) * mm});
            skLineSegment(sketch, "E558", {"start": v(27.66, 4.36) * mm, "end": v(27.56, 4.37) * mm});
            skLineSegment(sketch, "E559", {"start": v(27.56, 4.37) * mm, "end": v(27.46, 4.38) * mm});
            skLineSegment(sketch, "E560", {"start": v(27.46, 4.38) * mm, "end": v(27.36, 4.38) * mm});
            skLineSegment(sketch, "E561", {"start": v(27.36, 4.38) * mm, "end": v(27.15, 4.37) * mm});
            skLineSegment(sketch, "E562", {"start": v(27.15, 4.37) * mm, "end": v(26.94, 4.35) * mm});
            skLineSegment(sketch, "E563", {"start": v(26.94, 4.35) * mm, "end": v(26.74, 4.3) * mm});
            skLineSegment(sketch, "E564", {"start": v(26.74, 4.3) * mm, "end": v(26.54, 4.24) * mm});
            skLineSegment(sketch, "E565", {"start": v(26.54, 4.24) * mm, "end": v(26.34, 4.17) * mm});
            skLineSegment(sketch, "E566", {"start": v(26.34, 4.17) * mm, "end": v(26.14, 4.07) * mm});
            skLineSegment(sketch, "E567", {"start": v(26.14, 4.07) * mm, "end": v(25.95, 3.96) * mm});
            skLineSegment(sketch, "E568", {"start": v(25.95, 3.96) * mm, "end": v(25.76, 3.83) * mm});
            skLineSegment(sketch, "E569", {"start": v(25.76, 3.83) * mm, "end": v(25.58, 3.7) * mm});
            skLineSegment(sketch, "E570", {"start": v(25.58, 3.7) * mm, "end": v(25.4, 3.55) * mm});
            skLineSegment(sketch, "E571", {"start": v(25.4, 3.55) * mm, "end": v(25.22, 3.39) * mm});
            skLineSegment(sketch, "E572", {"start": v(25.22, 3.39) * mm, "end": v(25.05, 3.22) * mm});
            skLineSegment(sketch, "E573", {"start": v(25.05, 3.22) * mm, "end": v(24.88, 3.04) * mm});
            skLineSegment(sketch, "E574", {"start": v(24.88, 3.04) * mm, "end": v(24.56, 2.66) * mm});
            skLineSegment(sketch, "E575", {"start": v(24.56, 2.66) * mm, "end": v(24.41, 2.45) * mm});
            skLineSegment(sketch, "E576", {"start": v(24.41, 2.45) * mm, "end": v(24.13, 2.01) * mm});
            skLineSegment(sketch, "E577", {"start": v(24.13, 2.01) * mm, "end": v(23.86, 1.55) * mm});
            skLineSegment(sketch, "E578", {"start": v(23.86, 1.55) * mm, "end": v(23.62, 1.06) * mm});
            skLineSegment(sketch, "E579", {"start": v(23.62, 1.06) * mm, "end": v(23.4, 0.54) * mm});
            skLineSegment(sketch, "E580", {"start": v(23.4, 0.54) * mm, "end": v(23.2, 0.01) * mm});
            skLineSegment(sketch, "E581", {"start": v(23.2, 0.01) * mm, "end": v(23.04, -0.5) * mm});
            skLineSegment(sketch, "E582", {"start": v(23.04, -0.5) * mm, "end": v(22.9, -1.03) * mm});
            skLineSegment(sketch, "E583", {"start": v(22.9, -1.03) * mm, "end": v(22.8, -1.55) * mm});
            skSolve(sketch);
        }
        {
            var Q0;
            Q0=makeQuery(id+"F0.imprint","IMPRINT",FACE,{"disambiguationData":[TD([[makeQuery(id+"F0.imprint","IMPRINT",EDGE,{"derivedFrom":sQuery(id+"F0.wireOp",EDGE,"E170")}),-1.0]])]});
            var Q1;
            {var subQ1=sQuery(id+"F0.wireOp",EDGE,"E3");Q1=makeQuery(id+"F0.imprint","IMPRINT",FACE,{"disambiguationData":[TD([[makeQuery(id+"F0.imprint","IMPRINT",EDGE,{"derivedFrom":subQ1}),-1.0]])]});}
            var Q2;
            Q2=makeQuery(id+"F0.imprint","IMPRINT",FACE,{"disambiguationData":[TD([[makeQuery(id+"F0.imprint","IMPRINT",EDGE,{"derivedFrom":sQuery(id+"F0.wireOp",EDGE,"E21")}),1.0]])]});
            var Q3;
            Q3=makeQuery(id+"F0.imprint","IMPRINT",FACE,{"disambiguationData":[TD([[makeQuery(id+"F0.imprint","IMPRINT",EDGE,{"derivedFrom":sQuery(id+"F0.wireOp",EDGE,"E24")}),-1.0]])]});
            var Q4;
            Q4=makeQuery(id+"F0.imprint","IMPRINT",FACE,{"disambiguationData":[TD([[makeQuery(id+"F0.imprint","IMPRINT",EDGE,{"derivedFrom":sQuery(id+"F0.wireOp",EDGE,"E1")}),1.0]])]});
            var Q5;
            Q5=makeQuery(id+"F0.imprint","IMPRINT",FACE,{"disambiguationData":[TD([[makeQuery(id+"F0.imprint","IMPRINT",EDGE,{"derivedFrom":sQuery(id+"F0.wireOp",EDGE,"E5")}),-1.0]])]});
            var Q6;
            Q6=makeQuery(id+"F0.imprint","IMPRINT",FACE,{"disambiguationData":[TD([[makeQuery(id+"F0.imprint","IMPRINT",EDGE,{"derivedFrom":sQuery(id+"F0.wireOp",EDGE,"E501")}),1.0]])]});
            var Q7;
            Q7=makeQuery(id+"F0.imprint","IMPRINT",FACE,{"disambiguationData":[TD([[makeQuery(id+"F0.imprint","IMPRINT",EDGE,{"derivedFrom":sQuery(id+"F0.wireOp",EDGE,"E316")}),-1.0]])]});
            extrude(context, id + "F1", {"entities" : qUnion([Q0, Q1, Q2, Q3, Q4, Q5, Q6, Q7]), "oppositeDirection" : true, "depth" : 1.6 * mm, "offsetDistance" : 25 * mm});
        }
        {
            var Q0;
            Q0=makeQuery(id+"F0.imprint","IMPRINT",FACE,{"disambiguationData":[TD([[makeQuery(id+"F0.imprint","IMPRINT",EDGE,{"derivedFrom":sQuery(id+"F0.wireOp",EDGE,"E1")}),1.0]])]});
            extrude(context, id + "F2", {"entities" : qUnion([Q0]), "operationType" : NewBodyOperationType.ADD, "depth" : 1.6 * mm, "offsetDistance" : 25 * mm});
        }
        {
            var Q0;
            Q0=makeQuery(id+"F0.imprint","IMPRINT",FACE,{"disambiguationData":[TD([[makeQuery(id+"F0.imprint","IMPRINT",EDGE,{"derivedFrom":sQuery(id+"F0.wireOp",EDGE,"E5")}),-1.0]])]});
            var Q1;
            Q1=makeQuery(id+"F0.imprint","IMPRINT",FACE,{"disambiguationData":[TD([[makeQuery(id+"F0.imprint","IMPRINT",EDGE,{"derivedFrom":sQuery(id+"F0.wireOp",EDGE,"E24")}),-1.0]])]});
            var Q2;
            Q2=makeQuery(id+"F0.imprint","IMPRINT",FACE,{"disambiguationData":[TD([[makeQuery(id+"F0.imprint","IMPRINT",EDGE,{"derivedFrom":sQuery(id+"F0.wireOp",EDGE,"E170")}),-1.0]])]});
            var Q3;
            Q3=makeQuery(id+"F0.imprint","IMPRINT",FACE,{"disambiguationData":[TD([[makeQuery(id+"F0.imprint","IMPRINT",EDGE,{"derivedFrom":sQuery(id+"F0.wireOp",EDGE,"E316")}),-1.0]])]});
            extrude(context, id + "F3", {"entities" : qUnion([Q0, Q1, Q2, Q3]), "operationType" : NewBodyOperationType.ADD, "depth" : 1 * mm, "offsetDistance" : 25 * mm});
        }
    });
